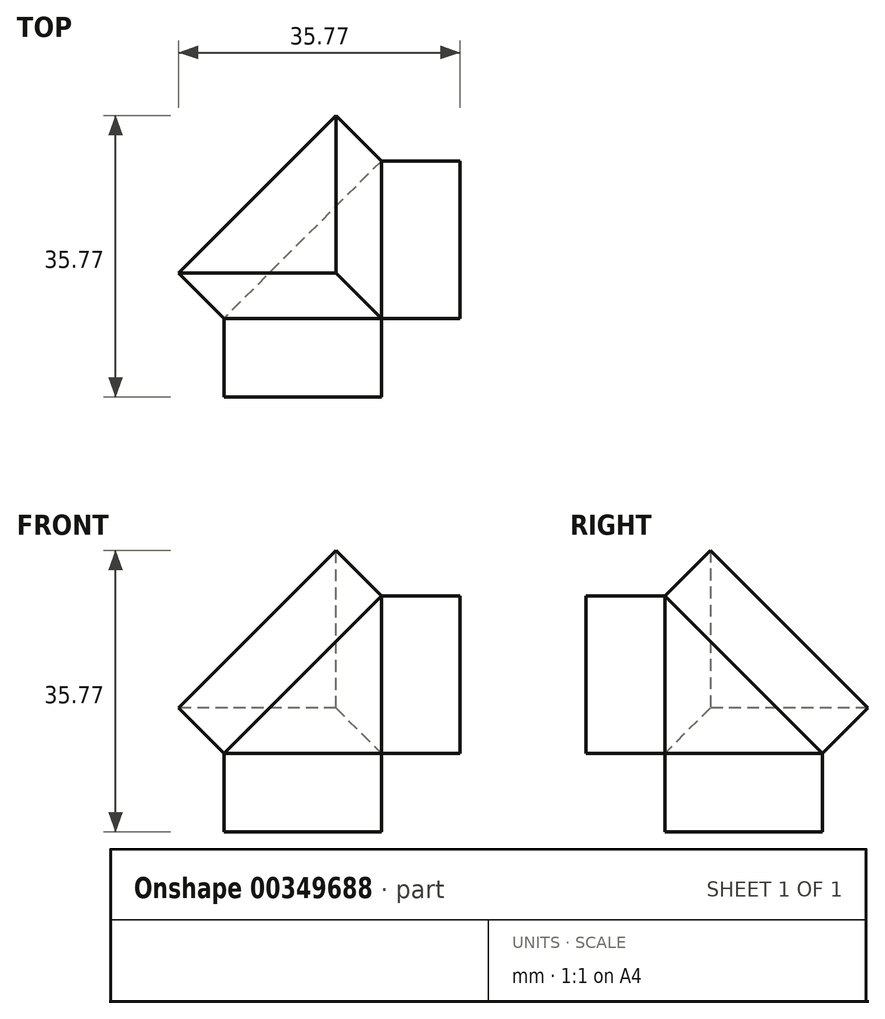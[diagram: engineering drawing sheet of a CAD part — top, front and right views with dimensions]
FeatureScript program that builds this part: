
annotation { "Feature Type Name" : "Feature", "Feature Type Description" : "" }
export const myFeature = defineFeature(function(context is Context, id is Id, definition is map)
    precondition{}
    {
        {
            var Q0;
            Q0=qCreatedBy(makeId("Top.planeOp"),FACE);
            var sketch = newSketch(context, id + "F0", { "sketchPlane" : qUnion([Q0])});
            skLineSegment(sketch, "E0.bottom", {"start": v(10, 10) * mm, "end": v(-10, 10) * mm});
            skLineSegment(sketch, "E0.top", {"start": v(10, -10) * mm, "end": v(-10, -10) * mm});
            skLineSegment(sketch, "E0.left", {"start": v(10, 10) * mm, "end": v(10, -10) * mm});
            skLineSegment(sketch, "E0.right", {"start": v(-10, 10) * mm, "end": v(-10, -10) * mm});
            skPoint(sketch, "E0.middle", {"position": v(0, 0) * mm});
            skSolve(sketch);
        }
        {
            var Q0;
            Q0=makeQuery(id+"F0.imprint","IMPRINT",FACE,{"disambiguationData":[TD([[makeQuery(id+"F0.imprint","IMPRINT",EDGE,{"derivedFrom":sQuery(id+"F0.wireOp",EDGE,"E0.bottom")}),1.0]])]});
            extrude(context, id + "F1", {"entities" : qUnion([Q0]), "depth" : 20 * mm});
        }
        {
            var Q0;
            Q0=makeQuery(id+"F1.opExtrude","SWEPT_EDGE",EDGE,{"disambiguationData":[OSD([sQuery(id+"F0.wireOp",EDGE,"E0.bottom"),sQuery(id+"F0.wireOp",EDGE,"E0.right")])]});
            var Q1;
            Q1=makeQuery(id+"F1.opExtrude","CAP_EDGE",EDGE,{"disambiguationData":[OSD([sQuery(id+"F0.wireOp",EDGE,"E0.right")])],"isStart":false});
            var Q2;
            Q2=makeQuery(id+"F1.opExtrude","CAP_EDGE",EDGE,{"disambiguationData":[OSD([sQuery(id+"F0.wireOp",EDGE,"E0.bottom")])],"isStart":false});
            chamfer(context, id + "F2", {"entities" : qUnion([Q0, Q1, Q2]), "width" : 20 * mm, "tangentPropagation" : true});
        }
        {
            var Q0;
            Q0=makeQuery(id+"F1.opExtrude","SWEPT_FACE",FACE,{"disambiguationData":[OSD([sQuery(id+"F0.wireOp",EDGE,"E0.left")])]});
            var sketch = newSketch(context, id + "F3", { "sketchPlane" : qUnion([Q0])});
            skSolve(sketch);
        }
        {
            var Q0;
            Q0 = qSketchRegion(id + "F3", true);
            var Q1;
            {var subQ0=sQuery(id+"F0.wireOp",EDGE,"E0.left");Q1=makeQuery(id+"F3.imprint","IMPRINT",FACE,{"disambiguationData":[TD([[makeQuery(id+"F3.imprint","IMPRINT",EDGE,{"derivedFrom":makeQuery(id+"F1.opExtrude","CAP_EDGE",EDGE,{"disambiguationData":[OSD([subQ0])],"isStart":true})}),-1.0]])]});}
            extrude(context, id + "F4", {"entities" : qUnion([Q0, Q1]), "operationType" : NewBodyOperationType.ADD, "depth" : 10 * mm});
        }
        {
            var Q0;
            {var subQ0=sQuery(id+"F0.wireOp",EDGE,"E0.left");Q0=makeQuery(id+"F4.boolean.opBoolean","MERGE",FACE,{"derivedFrom":[makeQuery(id+"F1.opExtrude","CAP_FACE",FACE,{"disambiguationData":[OSD([sQuery(id+"F0.wireOp",EDGE,"E0.bottom"),sQuery(id+"F0.wireOp",EDGE,"E0.top"),subQ0,sQuery(id+"F0.wireOp",EDGE,"E0.right")])],"isStart":true}),makeQuery(id+"F4.opExtrude","SWEPT_FACE",FACE,{"disambiguationData":[OSD([subQ0])]})]});}
            var sketch = newSketch(context, id + "F5", { "sketchPlane" : qUnion([Q0])});
            skLineSegment(sketch, "E1", {"start": v(10, -10) * mm, "end": v(10, 10) * mm});
            skSolve(sketch);
        }
        {
            var Q0;
            {var subQ0=sQuery(id+"F5.wireOp",EDGE,"E1");Q0=makeQuery(id+"F5.imprint","IMPRINT",FACE,{"disambiguationData":[TD([[makeQuery(id+"F5.imprint","IMPRINT",EDGE,{"derivedFrom":subQ0}),1.0]])]});}
            extrude(context, id + "F6", {"entities" : qUnion([Q0]), "operationType" : NewBodyOperationType.ADD, "depth" : 10 * mm});
        }
        {
            var Q0;
            {var subQ0=sQuery(id+"F0.wireOp",EDGE,"E0.left");var subQ1=sQuery(id+"F0.wireOp",EDGE,"E0.top");Q0=makeQuery(id+"F6.boolean.opBoolean","MERGE",FACE,{"derivedFrom":[makeQuery(id+"F4.boolean.opBoolean","MERGE",FACE,{"derivedFrom":[makeQuery(id+"F1.opExtrude","SWEPT_FACE",FACE,{"disambiguationData":[OSD([subQ1])]}),makeQuery(id+"F4.opExtrude","SWEPT_FACE",FACE,{"disambiguationData":[OSD([subQ1,subQ0])]})]}),makeQuery(id+"F6.opExtrude","SWEPT_FACE",FACE,{"disambiguationData":[OSD([subQ1,subQ0])]})]});}
            var sketch = newSketch(context, id + "F7", { "sketchPlane" : qUnion([Q0])});
            skLineSegment(sketch, "E2", {"start": v(10, 0) * mm, "end": v(-10, 0) * mm});
            skLineSegment(sketch, "E3", {"start": v(10, 0) * mm, "end": v(10, 20) * mm});
            skSolve(sketch);
        }
        {
            var Q0;
            Q0=makeQuery(id+"F7.imprint","IMPRINT",FACE,{"disambiguationData":[TD([[makeQuery(id+"F7.imprint","IMPRINT",EDGE,{"derivedFrom":sQuery(id+"F7.wireOp",EDGE,"E2")}),-1.0]])]});
            extrude(context, id + "F8", {"entities" : qUnion([Q0]), "operationType" : NewBodyOperationType.ADD, "depth" : 10 * mm});
        }
        {
            var Q0;
            Q0=makeQuery(id+"F2.opChamfer","BLEND_FACE",FACE,{"disambiguationData":[OSD([sQuery(id+"F0.wireOp",EDGE,"E0.bottom"),sQuery(id+"F0.wireOp",EDGE,"E0.right")])]});
            extrude(context, id + "F9", {"entities" : qUnion([Q0]), "operationType" : NewBodyOperationType.ADD, "depth" : 10 * mm});
        }
    });
